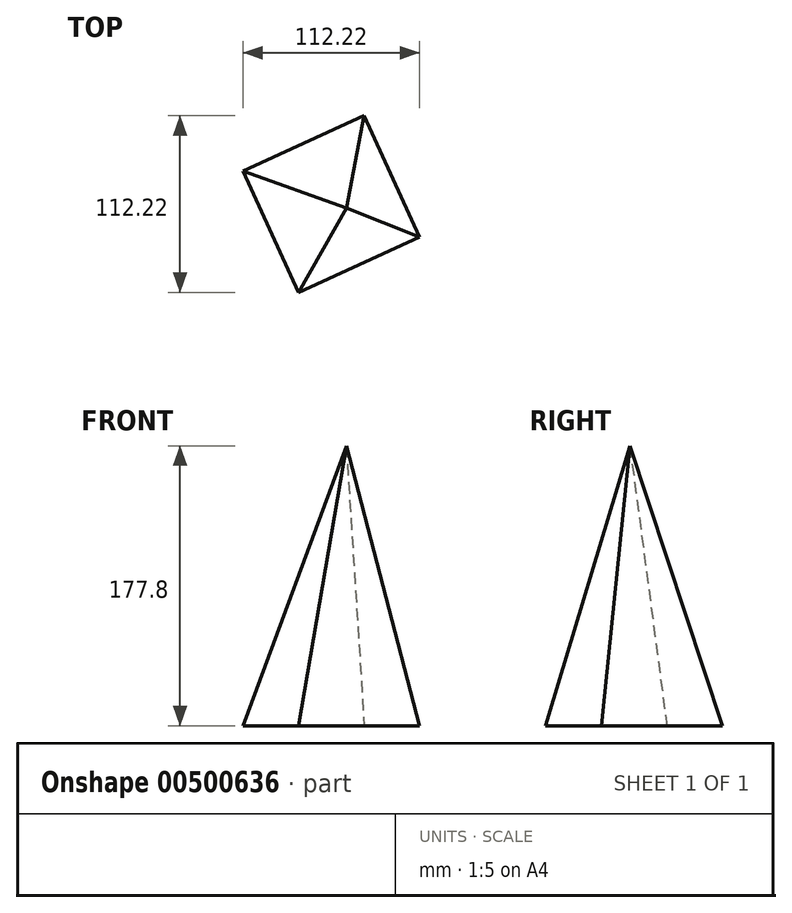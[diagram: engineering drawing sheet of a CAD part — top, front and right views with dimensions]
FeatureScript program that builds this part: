
annotation { "Feature Type Name" : "Feature", "Feature Type Description" : "" }
export const myFeature = defineFeature(function(context is Context, id is Id, definition is map)
    precondition{}
    {
        {
            var Q0;
            Q0=qCreatedBy(makeId("Top.planeOp"),FACE);
            var sketch = newSketch(context, id + "F0", { "sketchPlane" : qUnion([Q0])});
            skCircle(sketch, "E0.cCircle", {"center": v(0, 0) * mm, "radius": 42.32 * mm, "construction": true});
            skLineSegment(sketch, "E0.0", {"start": v(20.84, 56.1) * mm, "end": v(56.1, -20.84) * mm});
            skLineSegment(sketch, "E0.1", {"start": v(56.1, -20.84) * mm, "end": v(-20.84, -56.1) * mm});
            skLineSegment(sketch, "E0.2", {"start": v(-20.84, -56.1) * mm, "end": v(-56.1, 20.84) * mm});
            skLineSegment(sketch, "E0.3", {"start": v(-56.1, 20.84) * mm, "end": v(20.84, 56.1) * mm});
            skPoint(sketch, "E0.0.midPoint", {"position": v(38.47, 17.63) * mm});
            skSolve(sketch);
        }
        {
            var Q0;
            Q0=qCreatedBy(makeId("Top.planeOp"),FACE);
            cPlane(context, id + "F1", {"entities" : qUnion([Q0]), "cplaneType" : CPlaneType.OFFSET, "offset" : 177.8 * mm, "width" : 152.4 * mm, "height" : 152.4 * mm});
        }
        {
            var Q0;
            Q0=qCreatedBy(id+"F1.planeOp",FACE);
            var sketch = newSketch(context, id + "F2", { "sketchPlane" : qUnion([Q0])});
            skPoint(sketch, "E1", {"position": v(9.46, -2.7) * mm});
            skSolve(sketch);
        }
        {
            var Q0;
            Q0=sQuery(id+"F2.wireOp",VERTEX,"E1");
            var Q1;
            Q1=makeQuery(id+"F0.imprint","IMPRINT",FACE,{"disambiguationData":[TD([[makeQuery(id+"F0.imprint","IMPRINT",EDGE,{"derivedFrom":sQuery(id+"F0.wireOp",EDGE,"E0.0")}),-1.0]])]});
            loft(context, id + "F3", {"sheetProfilesArray" : [{ "sheetProfileEntities" : qUnion([Q0]) }, { "sheetProfileEntities" : qUnion([Q1]) }]});
        }
    });
